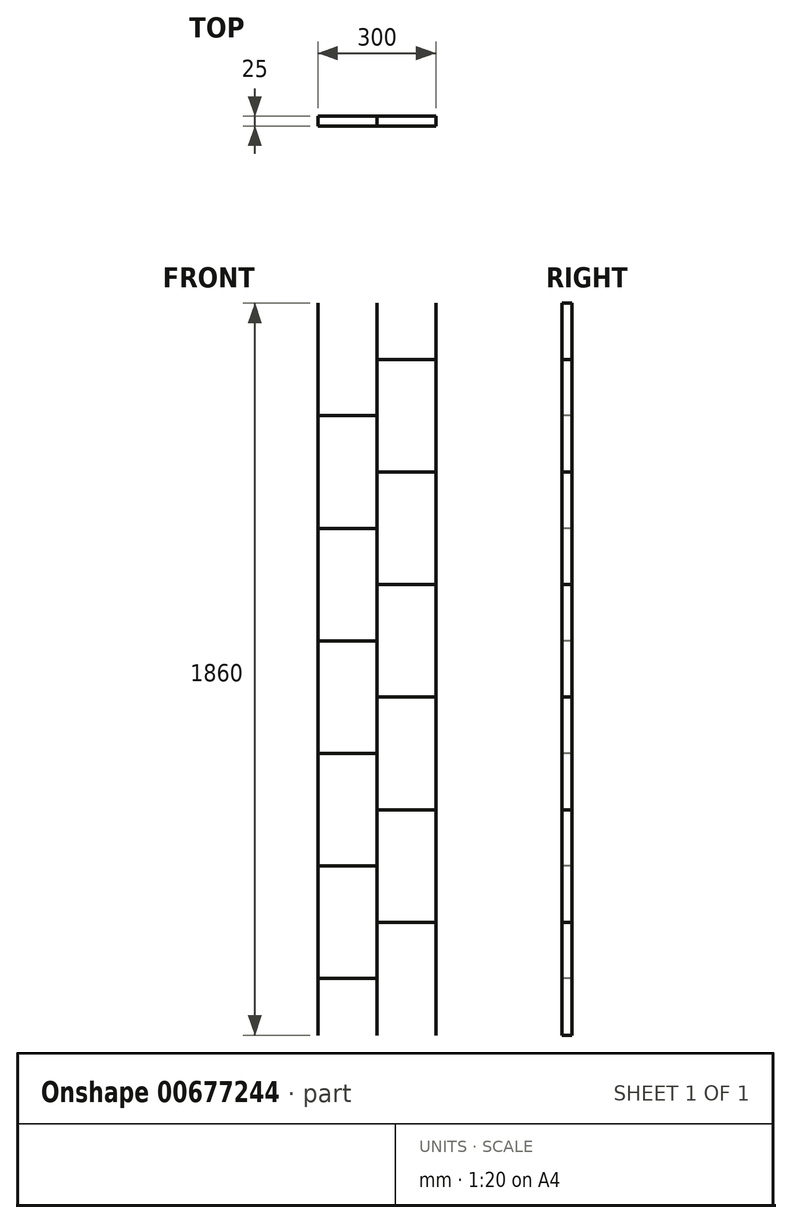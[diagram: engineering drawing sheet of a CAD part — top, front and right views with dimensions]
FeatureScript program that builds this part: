
annotation { "Feature Type Name" : "Feature", "Feature Type Description" : "" }
export const myFeature = defineFeature(function(context is Context, id is Id, definition is map)
    precondition{}
    {
        {
            var Q0;
            Q0=qCreatedBy(makeId("Front.planeOp"),FACE);
            var sketch = newSketch(context, id + "F0", { "sketchPlane" : qUnion([Q0])});
            skLineSegment(sketch, "E0.bottom", {"start": v(-500, 1187.8) * mm, "end": v(0, 1187.8) * mm});
            skLineSegment(sketch, "E0.top", {"start": v(-500, -672.2) * mm, "end": v(0, -672.2) * mm});
            skLineSegment(sketch, "E0.left", {"start": v(-500, 1187.8) * mm, "end": v(-500, -672.2) * mm});
            skLineSegment(sketch, "E0.right", {"start": v(0, 1187.8) * mm, "end": v(0, -672.2) * mm});
            skLineSegment(sketch, "E1", {"start": v(-400, 1187.8) * mm, "end": v(-400, -672.2) * mm});
            skLineSegment(sketch, "E2", {"start": v(-250, 1187.8) * mm, "end": v(-250, -672.2) * mm});
            skLineSegment(sketch, "E3", {"start": v(-100, 1187.8) * mm, "end": v(-100, -672.2) * mm});
            skLineSegment(sketch, "E4", {"start": v(-100, 758.8) * mm, "end": v(-250, 758.8) * mm});
            skLineSegment(sketch, "E5", {"start": v(-100, 1044.8) * mm, "end": v(-250, 1044.8) * mm});
            skLineSegment(sketch, "E6", {"start": v(-100, 472.8) * mm, "end": v(-250, 472.8) * mm});
            skLineSegment(sketch, "E7", {"start": v(-100, 186.8) * mm, "end": v(-250, 186.8) * mm});
            skLineSegment(sketch, "E8", {"start": v(-100, -99.2) * mm, "end": v(-250, -99.2) * mm});
            skLineSegment(sketch, "E9", {"start": v(-100, -385.2) * mm, "end": v(-250, -385.2) * mm});
            skLineSegment(sketch, "E10", {"start": v(-400, -528.2) * mm, "end": v(-250, -528.2) * mm});
            skLineSegment(sketch, "E11", {"start": v(-400, -242.2) * mm, "end": v(-250, -242.2) * mm});
            skLineSegment(sketch, "E12", {"start": v(-400, 43.8) * mm, "end": v(-250, 43.8) * mm});
            skLineSegment(sketch, "E13", {"start": v(-400, 329.8) * mm, "end": v(-250, 329.8) * mm});
            skLineSegment(sketch, "E14", {"start": v(-400, 615.8) * mm, "end": v(-250, 615.8) * mm});
            skLineSegment(sketch, "E15", {"start": v(-400, 901.8) * mm, "end": v(-250, 901.8) * mm});
            skSolve(sketch);
        }
        {
            var Q0;
            Q0=sQuery(id+"F0.wireOp",EDGE,"E15");
            var Q1;
            Q1=sQuery(id+"F0.wireOp",EDGE,"E14");
            var Q2;
            Q2=sQuery(id+"F0.wireOp",EDGE,"E13");
            var Q3;
            Q3=sQuery(id+"F0.wireOp",EDGE,"E12");
            var Q4;
            Q4=sQuery(id+"F0.wireOp",EDGE,"E11");
            var Q5;
            Q5=sQuery(id+"F0.wireOp",EDGE,"E10");
            var Q6;
            Q6=sQuery(id+"F0.wireOp",EDGE,"E9");
            var Q7;
            Q7=sQuery(id+"F0.wireOp",EDGE,"E8");
            var Q8;
            Q8=sQuery(id+"F0.wireOp",EDGE,"E7");
            var Q9;
            Q9=sQuery(id+"F0.wireOp",EDGE,"E6");
            var Q10;
            Q10=sQuery(id+"F0.wireOp",EDGE,"E4");
            var Q11;
            Q11=sQuery(id+"F0.wireOp",EDGE,"E5");
            extrude(context, id + "F1", {"bodyType" : ToolBodyType.SURFACE, "surfaceEntities" : qUnion([Q0, Q1, Q2, Q3, Q4, Q5, Q6, Q7, Q8, Q9, Q10, Q11]), "depth" : 25 * mm, "offsetDistance" : 25 * mm});
        }
        {
            var Q0;
            Q0=sQuery(id+"F0.wireOp",EDGE,"E3");
            var Q1;
            Q1=sQuery(id+"F0.wireOp",EDGE,"E2");
            var Q2;
            Q2=sQuery(id+"F0.wireOp",EDGE,"E1");
            extrude(context, id + "F2", {"bodyType" : ToolBodyType.SURFACE, "surfaceEntities" : qUnion([Q0, Q1, Q2]), "depth" : 25 * mm, "offsetDistance" : 25 * mm});
        }
    });
